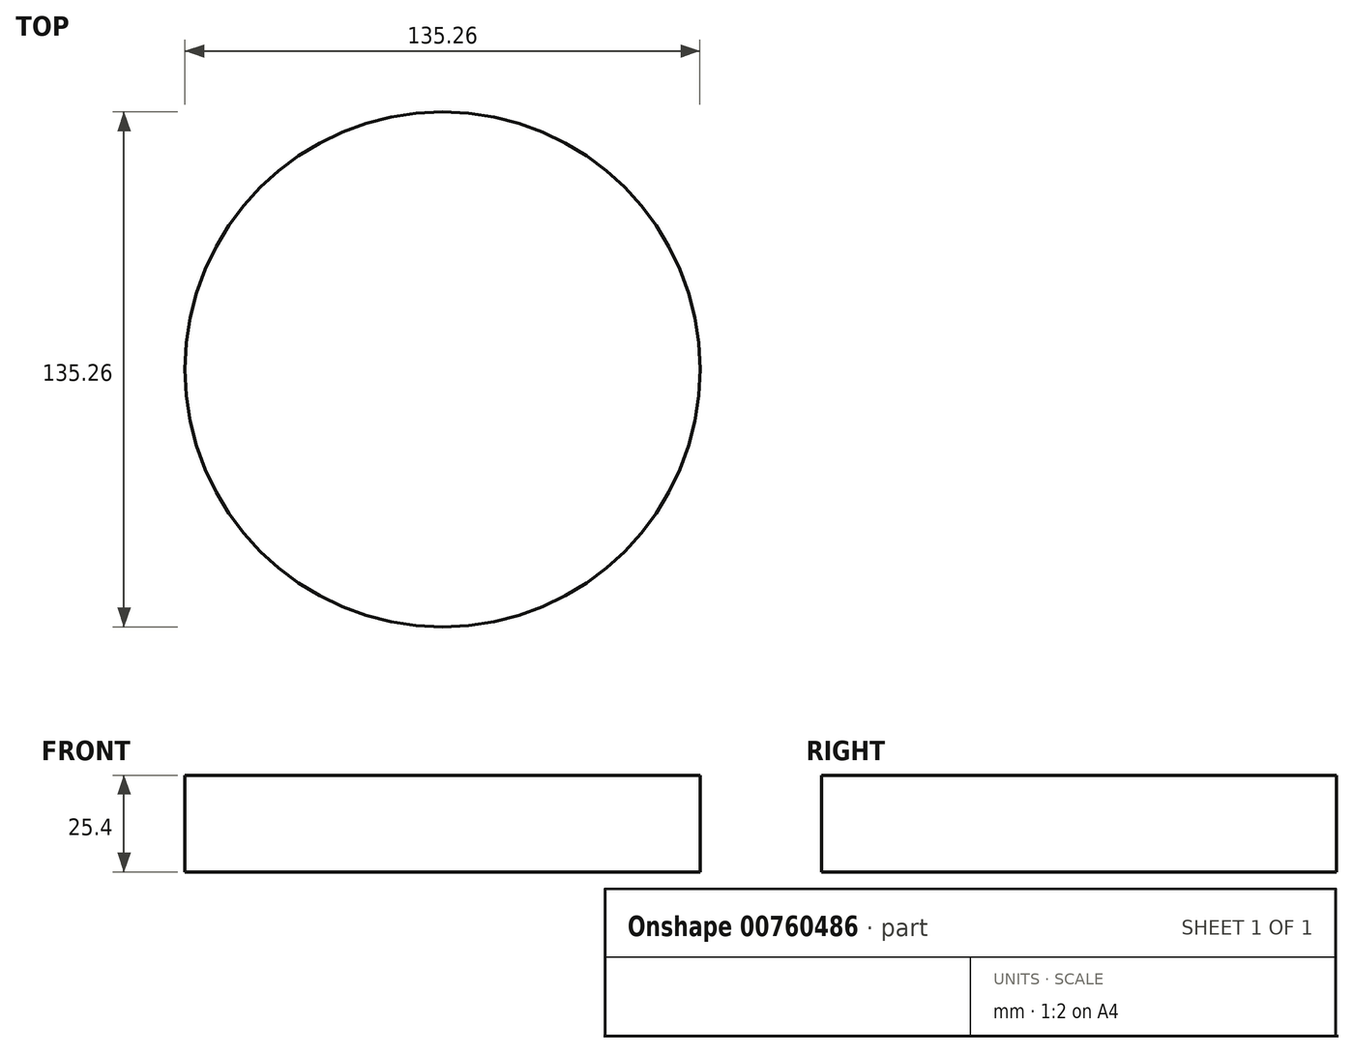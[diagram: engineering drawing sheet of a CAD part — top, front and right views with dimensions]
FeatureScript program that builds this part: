
annotation { "Feature Type Name" : "Feature", "Feature Type Description" : "" }
export const myFeature = defineFeature(function(context is Context, id is Id, definition is map)
    precondition{}
    {
        {
            var Q0;
            Q0=qCreatedBy(makeId("Top.planeOp"),FACE);
            var sketch = newSketch(context, id + "F0", { "sketchPlane" : qUnion([Q0])});
            skCircle(sketch, "E0", {"center": v(0, 0) * mm, "radius": 67.63 * mm});
            skSolve(sketch);
        }
        {
            var Q0;
            Q0=makeQuery(id+"F0.imprint","IMPRINT",FACE,{"disambiguationData":[TD([[makeQuery(id+"F0.imprint","IMPRINT",EDGE,{"derivedFrom":sQuery(id+"F0.wireOp",EDGE,"E0")}),1.0]])]});
            extrude(context, id + "F1", {"entities" : qUnion([Q0]), "depth" : 25.4 * mm, "offsetDistance" : 25.4 * mm});
        }
    });
